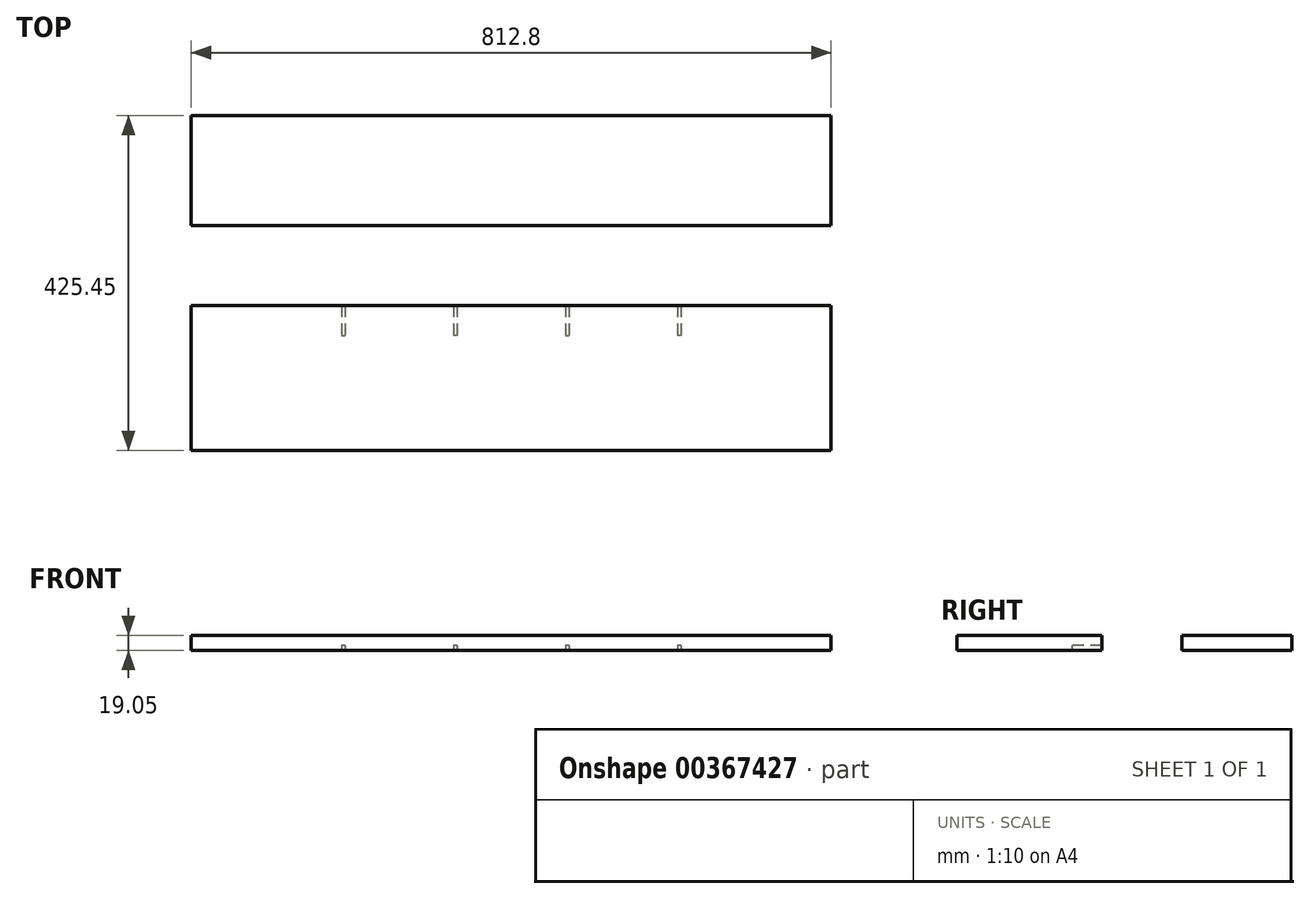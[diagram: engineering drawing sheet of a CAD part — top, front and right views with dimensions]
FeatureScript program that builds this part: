
annotation { "Feature Type Name" : "Feature", "Feature Type Description" : "" }
export const myFeature = defineFeature(function(context is Context, id is Id, definition is map)
    precondition{}
    {
        {
            var Q0;
            Q0=qCreatedBy(makeId("Top.planeOp"),FACE);
            var sketch = newSketch(context, id + "F0", { "sketchPlane" : qUnion([Q0])});
            skLineSegment(sketch, "E0.bottom", {"start": v(406.4, 69.85) * mm, "end": v(-406.4, 69.85) * mm});
            skLineSegment(sketch, "E0.top", {"start": v(406.4, -69.85) * mm, "end": v(-406.4, -69.85) * mm});
            skLineSegment(sketch, "E0.left", {"start": v(406.4, 69.85) * mm, "end": v(406.4, -69.85) * mm});
            skLineSegment(sketch, "E0.right", {"start": v(-406.4, 69.85) * mm, "end": v(-406.4, -69.85) * mm});
            skPoint(sketch, "E0.middle", {"position": v(0, 0) * mm});
            skSolve(sketch);
        }
        {
            var Q0;
            Q0 = qSketchRegion(id + "F0", true);
            extrude(context, id + "F1", {"entities" : qUnion([Q0]), "depth" : 19.05 * mm});
        }
        {
            var Q0;
            Q0=qCreatedBy(makeId("Top.planeOp"),FACE);
            var sketch = newSketch(context, id + "F2", { "sketchPlane" : qUnion([Q0])});
            skLineSegment(sketch, "E1.bottom", {"start": v(406.4, -171.45) * mm, "end": v(-406.4, -171.45) * mm});
            skLineSegment(sketch, "E1.top", {"start": v(406.4, -355.6) * mm, "end": v(-406.4, -355.6) * mm});
            skLineSegment(sketch, "E1.left", {"start": v(406.4, -171.45) * mm, "end": v(406.4, -355.6) * mm});
            skLineSegment(sketch, "E1.right", {"start": v(-406.4, -171.45) * mm, "end": v(-406.4, -355.6) * mm});
            skPoint(sketch, "E1.middle", {"position": v(0, -263.53) * mm});
            skSolve(sketch);
        }
        {
            var Q0;
            Q0 = qSketchRegion(id + "F2", true);
            extrude(context, id + "F3", {"entities" : qUnion([Q0]), "depth" : 19.05 * mm});
        }
        {
            var Q0;
            Q0=makeQuery(id+"F3.opExtrude","CAP_FACE",FACE,{"disambiguationData":[OSD([sQuery(id+"F2.wireOp",EDGE,"E1.bottom"),sQuery(id+"F2.wireOp",EDGE,"E1.top"),sQuery(id+"F2.wireOp",EDGE,"E1.left"),sQuery(id+"F2.wireOp",EDGE,"E1.right")])],"isStart":true});
            var sketch = newSketch(context, id + "F4", { "sketchPlane" : qUnion([Q0])});
            skLineSegment(sketch, "E2.bottom", {"start": v(68.74, 171.45) * mm, "end": v(73.5, 171.45) * mm});
            skLineSegment(sketch, "E2.top", {"start": v(68.74, 209.55) * mm, "end": v(73.5, 209.55) * mm});
            skLineSegment(sketch, "E2.left", {"start": v(73.5, 171.45) * mm, "end": v(73.5, 209.55) * mm});
            skLineSegment(sketch, "E2.right", {"start": v(68.74, 171.45) * mm, "end": v(68.74, 209.55) * mm});
            skLineSegment(sketch, "E3", {"start": v(0, 263.53) * mm, "end": v(0, 355.6) * mm, "construction": true});
            skLineSegment(sketch, "E4", {"start": v(355.6, 171.45) * mm, "end": v(355.6, 355.6) * mm, "construction": true});
            skLineSegment(sketch, "E5", {"start": v(355.6, 263.53) * mm, "end": v(213.36, 263.53) * mm, "construction": true});
            skLineSegment(sketch, "E6", {"start": v(213.36, 263.53) * mm, "end": v(71.12, 263.53) * mm, "construction": true});
            skLineSegment(sketch, "E7", {"start": v(71.12, 263.53) * mm, "end": v(-71.12, 263.53) * mm, "construction": true});
            skPoint(sketch, "E7.endSnap0", {"position": v(0, 263.53) * mm});
            skLineSegment(sketch, "E8", {"start": v(-71.12, 263.53) * mm, "end": v(-213.36, 263.53) * mm, "construction": true});
            skLineSegment(sketch, "E9", {"start": v(213.36, 263.53) * mm, "end": v(213.36, 171.45) * mm, "construction": true});
            skLineSegment(sketch, "E10", {"start": v(71.12, 263.53) * mm, "end": v(71.12, 171.45) * mm, "construction": true});
            skLineSegment(sketch, "E11.bottom", {"start": v(215.74, 171.45) * mm, "end": v(210.98, 171.45) * mm});
            skLineSegment(sketch, "E11.top", {"start": v(215.74, 209.55) * mm, "end": v(210.98, 209.55) * mm});
            skLineSegment(sketch, "E11.left", {"start": v(215.74, 171.45) * mm, "end": v(215.74, 209.55) * mm});
            skLineSegment(sketch, "E11.right", {"start": v(210.98, 171.45) * mm, "end": v(210.98, 209.55) * mm});
            skLineSegment(sketch, "E12.MirrorCS", {"start": v(-215.74, 171.45) * mm, "end": v(-210.98, 171.45) * mm});
            skLineSegment(sketch, "E13.MirrorCS", {"start": v(-68.74, 171.45) * mm, "end": v(-73.5, 171.45) * mm});
            skLineSegment(sketch, "E14.MirrorCS", {"start": v(-68.74, 209.55) * mm, "end": v(-73.5, 209.55) * mm});
            skLineSegment(sketch, "E15.MirrorCS", {"start": v(-215.74, 209.55) * mm, "end": v(-210.98, 209.55) * mm});
            skLineSegment(sketch, "E16.MirrorCS", {"start": v(-215.74, 171.45) * mm, "end": v(-215.74, 209.55) * mm});
            skLineSegment(sketch, "E17.MirrorCS", {"start": v(-68.74, 171.45) * mm, "end": v(-68.74, 209.55) * mm});
            skLineSegment(sketch, "E18.MirrorCS", {"start": v(-213.36, 263.53) * mm, "end": v(-71.12, 263.53) * mm, "construction": true});
            skLineSegment(sketch, "E19.MirrorCS", {"start": v(-213.36, 263.53) * mm, "end": v(-213.36, 171.45) * mm, "construction": true});
            skLineSegment(sketch, "E20.MirrorCS", {"start": v(-73.5, 171.45) * mm, "end": v(-73.5, 209.55) * mm});
            skLineSegment(sketch, "E21.MirrorCS", {"start": v(-210.98, 171.45) * mm, "end": v(-210.98, 209.55) * mm});
            skLineSegment(sketch, "E22.MirrorCS", {"start": v(-71.12, 263.53) * mm, "end": v(-71.12, 171.45) * mm, "construction": true});
            skSolve(sketch);
        }
        {
            var Q0;
            Q0 = qSketchRegion(id + "F4", true);
            extrude(context, id + "F5", {"entities" : qUnion([Q0]), "operationType" : NewBodyOperationType.REMOVE, "oppositeDirection" : true, "depth" : 6.35 * mm});
        }
    });
